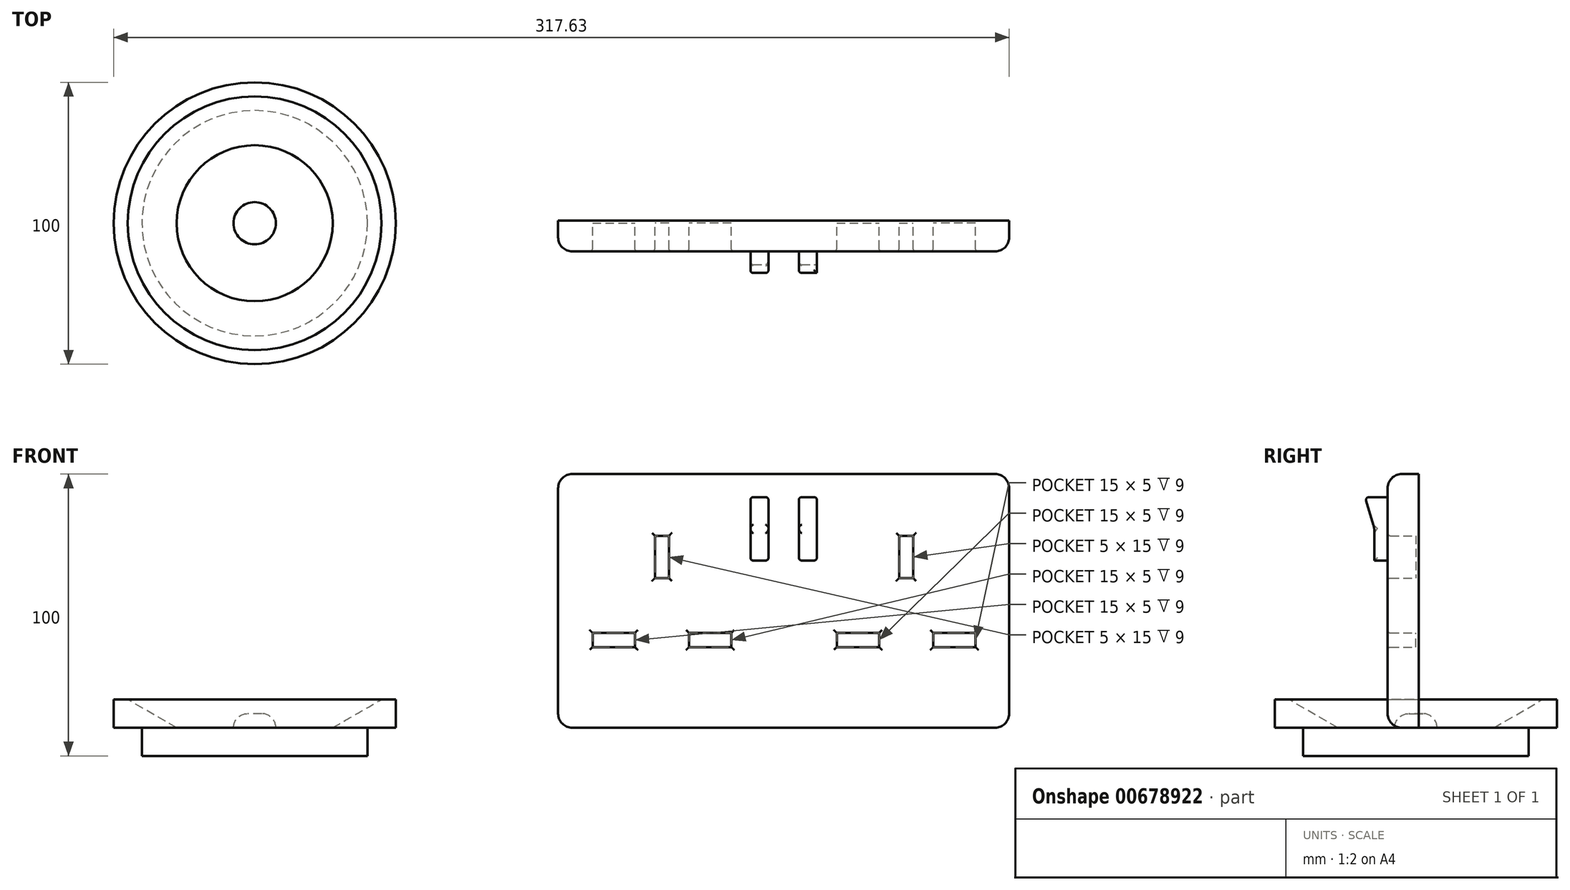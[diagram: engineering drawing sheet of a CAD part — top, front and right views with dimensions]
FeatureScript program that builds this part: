
annotation { "Feature Type Name" : "Feature", "Feature Type Description" : "" }
export const myFeature = defineFeature(function(context is Context, id is Id, definition is map)
    precondition{}
    {
        {
            var Q0;
            Q0=qCreatedBy(makeId("Top.planeOp"),FACE);
            var sketch = newSketch(context, id + "F0", { "sketchPlane" : qUnion([Q0])});
            skCircle(sketch, "E0", {"center": v(0, 0) * mm, "radius": 50 * mm});
            skSolve(sketch);
        }
        {
            var Q0;
            Q0=qSketchRegion(id+"F0",true);
            extrude(context, id + "F1", {"entities" : qUnion([Q0]), "depth" : 10 * mm, "offsetDistance" : 25 * mm});
        }
        {
            var Q0;
            Q0=makeQuery(id+"F1.opExtrude","CAP_FACE",FACE,{"disambiguationData":[OSD([sQuery(id+"F0.wireOp",EDGE,"E0")])],"isStart":true});
            var sketch = newSketch(context, id + "F2", { "sketchPlane" : qUnion([Q0])});
            skCircle(sketch, "E1", {"center": v(0, 0) * mm, "radius": 40 * mm});
            skSolve(sketch);
        }
        {
            var Q0;
            Q0=qSketchRegion(id+"F2",true);
            extrude(context, id + "F3", {"entities" : qUnion([Q0]), "operationType" : NewBodyOperationType.ADD, "depth" : 10 * mm, "offsetDistance" : 25 * mm});
        }
        {
            var Q0;
            Q0=makeQuery(id+"F1.opExtrude","CAP_FACE",FACE,{"disambiguationData":[OSD([sQuery(id+"F0.wireOp",EDGE,"E0")])],"isStart":false});
            var sketch = newSketch(context, id + "F4", { "sketchPlane" : qUnion([Q0])});
            skCircle(sketch, "E2", {"center": v(0, 0) * mm, "radius": 45 * mm});
            skSolve(sketch);
        }
        {
            var Q0;
            Q0=qSketchRegion(id+"F4",true);
            extrude(context, id + "F5", {"entities" : qUnion([Q0]), "operationType" : NewBodyOperationType.REMOVE, "oppositeDirection" : true, "depth" : 10 * mm, "offsetDistance" : 25 * mm, "hasDraft" : true, "draftAngle" : 60 * degree, "draftPullDirection" : true});
        }
        {
            var Q0;
            Q0=makeQuery(id+"F5.boolean.opBoolean","COPY",FACE,{"derivedFrom":makeQuery(id+"F5.opExtrude","CAP_FACE",FACE,{"disambiguationData":[OSD([sQuery(id+"F4.wireOp",EDGE,"E2")])],"isStart":false})});
            var sketch = newSketch(context, id + "F6", { "sketchPlane" : qUnion([Q0])});
            skCircle(sketch, "E3", {"center": v(0, 0) * mm, "radius": 7.5 * mm});
            skSolve(sketch);
        }
        {
            var Q0;
            Q0=qSketchRegion(id+"F6",true);
            extrude(context, id + "F7", {"entities" : qUnion([Q0]), "operationType" : NewBodyOperationType.ADD, "depth" : 5 * mm, "offsetDistance" : 25 * mm});
        }
        {
            var Q0;
            Q0=makeQuery(id+"F7.opExtrude","CAP_EDGE",EDGE,{"disambiguationData":[OSD([sQuery(id+"F6.wireOp",EDGE,"E3")])],"isStart":false});
            fillet(context, id + "F8", {"entities" : qUnion([Q0]), "radius" : 5 * mm, "tangentPropagation" : true, "allowEdgeOverflow" : false});
        }
        {
            var Q0;
            Q0=qCreatedBy(makeId("Front.planeOp"),FACE);
            var sketch = newSketch(context, id + "F9", { "sketchPlane" : qUnion([Q0])});
            skLineSegment(sketch, "E4.bottom", {"start": v(107.63, 0) * mm, "end": v(267.63, 0) * mm});
            skLineSegment(sketch, "E4.top", {"start": v(107.63, 90) * mm, "end": v(267.63, 90) * mm});
            skLineSegment(sketch, "E4.left", {"start": v(107.63, 0) * mm, "end": v(107.63, 90) * mm});
            skLineSegment(sketch, "E4.right", {"start": v(267.63, 0) * mm, "end": v(267.63, 90) * mm});
            skSolve(sketch);
        }
        {
            var Q0;
            Q0=qSketchRegion(id+"F9",true);
            extrude(context, id + "F10", {"entities" : qUnion([Q0]), "depth" : 10 * mm, "offsetDistance" : 25 * mm});
        }
        {
            var Q0;
            Q0=qCreatedBy(makeId("Front.planeOp"),FACE);
            var sketch = newSketch(context, id + "F11", { "sketchPlane" : qUnion([Q0])});
            skLineSegment(sketch, "E5.bottom", {"start": v(146.96, 68.1) * mm, "end": v(141.96, 68.1) * mm});
            skLineSegment(sketch, "E5.top", {"start": v(146.96, 53.1) * mm, "end": v(141.96, 53.1) * mm});
            skLineSegment(sketch, "E5.left", {"start": v(146.96, 68.1) * mm, "end": v(146.96, 53.1) * mm});
            skLineSegment(sketch, "E5.right", {"start": v(141.96, 68.1) * mm, "end": v(141.96, 53.1) * mm});
            skPoint(sketch, "E5.middle", {"position": v(144.46, 60.6) * mm});
            skLineSegment(sketch, "E6.bottom", {"start": v(119.85, 28.62) * mm, "end": v(134.85, 28.62) * mm});
            skLineSegment(sketch, "E6.top", {"start": v(119.85, 33.62) * mm, "end": v(134.85, 33.62) * mm});
            skLineSegment(sketch, "E6.left", {"start": v(119.85, 28.62) * mm, "end": v(119.85, 33.62) * mm});
            skLineSegment(sketch, "E6.right", {"start": v(134.85, 28.62) * mm, "end": v(134.85, 33.62) * mm});
            skPoint(sketch, "E6.middle", {"position": v(127.35, 31.12) * mm});
            skLineSegment(sketch, "E7.bottom", {"start": v(169.06, 28.62) * mm, "end": v(154.06, 28.62) * mm});
            skLineSegment(sketch, "E7.top", {"start": v(169.06, 33.62) * mm, "end": v(154.06, 33.62) * mm});
            skLineSegment(sketch, "E7.left", {"start": v(169.06, 28.62) * mm, "end": v(169.06, 33.62) * mm});
            skLineSegment(sketch, "E7.right", {"start": v(154.06, 28.62) * mm, "end": v(154.06, 33.62) * mm});
            skPoint(sketch, "E7.middle", {"position": v(161.56, 31.12) * mm});
            skPoint(sketch, "E8", {"position": v(134.85, 31.12) * mm});
            skLineSegment(sketch, "E9.MirrorCS", {"start": v(228.58, 68.1) * mm, "end": v(228.58, 53.1) * mm});
            skLineSegment(sketch, "E10.MirrorCS", {"start": v(228.58, 68.1) * mm, "end": v(233.58, 68.1) * mm});
            skLineSegment(sketch, "E11.MirrorCS", {"start": v(233.58, 68.1) * mm, "end": v(233.58, 53.1) * mm});
            skLineSegment(sketch, "E12.MirrorCS", {"start": v(228.58, 53.1) * mm, "end": v(233.58, 53.1) * mm});
            skLineSegment(sketch, "E13.MirrorCS", {"start": v(206.47, 28.62) * mm, "end": v(221.47, 28.62) * mm});
            skLineSegment(sketch, "E14.MirrorCS", {"start": v(206.47, 33.62) * mm, "end": v(221.47, 33.62) * mm});
            skLineSegment(sketch, "E15.MirrorCS", {"start": v(221.47, 28.62) * mm, "end": v(221.47, 33.62) * mm});
            skLineSegment(sketch, "E16.MirrorCS", {"start": v(206.47, 28.62) * mm, "end": v(206.47, 33.62) * mm});
            skPoint(sketch, "E17.MirrorP", {"position": v(213.97, 31.12) * mm});
            skLineSegment(sketch, "E18.MirrorCS", {"start": v(240.68, 28.62) * mm, "end": v(240.68, 33.62) * mm});
            skLineSegment(sketch, "E19.MirrorCS", {"start": v(255.68, 28.62) * mm, "end": v(255.68, 33.62) * mm});
            skLineSegment(sketch, "E20.MirrorCS", {"start": v(255.68, 28.62) * mm, "end": v(240.68, 28.62) * mm});
            skLineSegment(sketch, "E21.MirrorCS", {"start": v(255.68, 33.62) * mm, "end": v(240.68, 33.62) * mm});
            skPoint(sketch, "E22.MirrorP", {"position": v(248.18, 31.12) * mm});
            skPoint(sketch, "E23.MirrorP", {"position": v(240.68, 31.12) * mm});
            skSolve(sketch);
        }
        {
            var Q0;
            Q0=qSketchRegion(id+"F11",true);
            extrude(context, id + "F12", {"entities" : qUnion([Q0]), "operationType" : NewBodyOperationType.REMOVE, "depth" : 15 * mm, "offsetDistance" : 25 * mm});
        }
        {
            var Q0;
            Q0=makeQuery(id+"F10.opExtrude","CAP_FACE",FACE,{"disambiguationData":[OSD([sQuery(id+"F9.wireOp",EDGE,"E4.bottom"),sQuery(id+"F9.wireOp",EDGE,"E4.top"),sQuery(id+"F9.wireOp",EDGE,"E4.left"),sQuery(id+"F9.wireOp",EDGE,"E4.right")])],"isStart":false});
            var sketch = newSketch(context, id + "F13", { "sketchPlane" : qUnion([Q0])});
            skLineSegment(sketch, "E24.bottom", {"start": v(193.04, 81.81) * mm, "end": v(199.4, 81.81) * mm});
            skLineSegment(sketch, "E24.top", {"start": v(193.04, 59.31) * mm, "end": v(199.4, 59.31) * mm});
            skLineSegment(sketch, "E24.left", {"start": v(193.04, 81.81) * mm, "end": v(193.04, 59.31) * mm});
            skLineSegment(sketch, "E24.right", {"start": v(199.4, 81.81) * mm, "end": v(199.4, 59.31) * mm});
            skLineSegment(sketch, "E25.MirrorCS", {"start": v(182.22, 81.81) * mm, "end": v(175.86, 81.81) * mm});
            skLineSegment(sketch, "E26.MirrorCS", {"start": v(182.22, 81.81) * mm, "end": v(182.22, 59.31) * mm});
            skLineSegment(sketch, "E27.MirrorCS", {"start": v(175.86, 81.81) * mm, "end": v(175.86, 59.31) * mm});
            skLineSegment(sketch, "E28.MirrorCS", {"start": v(182.22, 59.31) * mm, "end": v(175.86, 59.31) * mm});
            skSolve(sketch);
        }
        {
            var Q0;
            Q0=qSketchRegion(id+"F13",true);
            extrude(context, id + "F14", {"entities" : qUnion([Q0]), "operationType" : NewBodyOperationType.ADD, "depth" : 8 * mm, "offsetDistance" : 25 * mm});
        }
        {
            var Q0;
            Q0=makeQuery(id+"F14.opExtrude","SWEPT_FACE",FACE,{"disambiguationData":[OSD([sQuery(id+"F13.wireOp",EDGE,"E24.right")])]});
            var sketch = newSketch(context, id + "F15", { "sketchPlane" : qUnion([Q0])});
            skLineSegment(sketch, "E29", {"start": v(-14.66, 70.56) * mm, "end": v(-18, 81.81) * mm});
            skLineSegment(sketch, "E30", {"start": v(-14.66, 70.56) * mm, "end": v(-14.66, 59.31) * mm});
            skPoint(sketch, "E30.endSnap0", {"position": v(-14, 59.31) * mm});
            skLineSegment(sketch, "E31", {"start": v(-14.66, 59.31) * mm, "end": v(-18, 59.31) * mm});
            skLineSegment(sketch, "E32", {"start": v(-18, 59.31) * mm, "end": v(-18, 81.81) * mm});
            skSolve(sketch);
        }
        {
            var Q0;
            Q0=qSketchRegion(id+"F15",true);
            extrude(context, id + "F16", {"entities" : qUnion([Q0]), "operationType" : NewBodyOperationType.REMOVE, "oppositeDirection" : true, "depth" : 25 * mm, "offsetDistance" : 25 * mm});
        }
        {
            var Q0;
            Q0=makeQuery(id+"F16.boolean.opBoolean","COPY",EDGE,{"derivedFrom":makeQuery(id+"F16.opExtrude","CAP_EDGE",EDGE,{"disambiguationData":[OSD([sQuery(id+"F15.wireOp",EDGE,"E30")])],"isStart":true})});
            var Q1;
            Q1=makeQuery(id+"F16.boolean.opBoolean","COPY",EDGE,{"derivedFrom":makeQuery(id+"F16.opExtrude","CAP_EDGE",EDGE,{"disambiguationData":[OSD([sQuery(id+"F15.wireOp",EDGE,"E29")])],"isStart":true})});
            var Q2;
            {var subQ0=sQuery(id+"F13.wireOp",EDGE,"E24.bottom");Q2=makeQuery(id+"F16.boolean.opBoolean","MERGE",EDGE,{"derivedFrom":[makeQuery(id+"F14.opExtrude","CAP_EDGE",EDGE,{"disambiguationData":[OSD([subQ0])],"isStart":false}),makeQuery(id+"F16.opExtrude","SWEPT_EDGE",EDGE,{"disambiguationData":[OSD([subQ0,sQuery(id+"F13.wireOp",EDGE,"E24.right"),sQuery(id+"F15.wireOp",EDGE,"E29"),sQuery(id+"F15.wireOp",EDGE,"E32")])]})]});}
            var Q3;
            Q3=makeQuery(id+"F16.boolean.opBoolean","INTERSECT",EDGE,{"derivedFrom":[makeQuery(id+"F14.opExtrude","SWEPT_FACE",FACE,{"disambiguationData":[OSD([sQuery(id+"F13.wireOp",EDGE,"E24.left")])]}),makeQuery(id+"F16.opExtrude","SWEPT_FACE",FACE,{"disambiguationData":[OSD([sQuery(id+"F15.wireOp",EDGE,"E29")])]})]});
            var Q4;
            Q4=makeQuery(id+"F16.boolean.opBoolean","INTERSECT",EDGE,{"derivedFrom":[makeQuery(id+"F14.opExtrude","SWEPT_FACE",FACE,{"disambiguationData":[OSD([sQuery(id+"F13.wireOp",EDGE,"E24.left")])]}),makeQuery(id+"F16.opExtrude","SWEPT_FACE",FACE,{"disambiguationData":[OSD([sQuery(id+"F15.wireOp",EDGE,"E30")])]})]});
            var Q5;
            {var subQ0=sQuery(id+"F13.wireOp",EDGE,"E24.top");var subQ1=sQuery(id+"F15.wireOp",EDGE,"E30");Q5=makeQuery(id+"F16.boolean.opBoolean","COPY",EDGE,{"disambiguationData":[topologyDisambiguationEdgeConnected([makeQuery(id+"F14.opExtrude","SWEPT_FACE",FACE,{"disambiguationData":[OSD([subQ0])]})])],"derivedFrom":makeQuery(id+"F16.opExtrude","SWEPT_EDGE",EDGE,{"disambiguationData":[OSD([subQ0,sQuery(id+"F13.wireOp",EDGE,"E24.right"),subQ1,sQuery(id+"F15.wireOp",EDGE,"E31")])]})});}
            var Q6;
            Q6=makeQuery(id+"F14.opExtrude","SWEPT_EDGE",EDGE,{"disambiguationData":[OSD([sQuery(id+"F13.wireOp",EDGE,"E24.bottom"),sQuery(id+"F13.wireOp",EDGE,"E24.right")])]});
            var Q7;
            Q7=makeQuery(id+"F14.opExtrude","SWEPT_EDGE",EDGE,{"disambiguationData":[OSD([sQuery(id+"F13.wireOp",EDGE,"E24.top"),sQuery(id+"F13.wireOp",EDGE,"E24.right")])]});
            var Q8;
            Q8=makeQuery(id+"F14.opExtrude","SWEPT_EDGE",EDGE,{"disambiguationData":[OSD([sQuery(id+"F13.wireOp",EDGE,"E24.top"),sQuery(id+"F13.wireOp",EDGE,"E24.left")])]});
            var Q9;
            Q9=makeQuery(id+"F14.opExtrude","SWEPT_EDGE",EDGE,{"disambiguationData":[OSD([sQuery(id+"F13.wireOp",EDGE,"E24.bottom"),sQuery(id+"F13.wireOp",EDGE,"E24.left")])]});
            var Q10;
            Q10=makeQuery(id+"F16.boolean.opBoolean","INTERSECT",EDGE,{"derivedFrom":[makeQuery(id+"F14.opExtrude","SWEPT_FACE",FACE,{"disambiguationData":[OSD([sQuery(id+"F13.wireOp",EDGE,"E26.MirrorCS")])]}),makeQuery(id+"F16.opExtrude","SWEPT_FACE",FACE,{"disambiguationData":[OSD([sQuery(id+"F15.wireOp",EDGE,"E30")])]})]});
            var Q11;
            Q11=makeQuery(id+"F16.boolean.opBoolean","INTERSECT",EDGE,{"derivedFrom":[makeQuery(id+"F14.opExtrude","SWEPT_FACE",FACE,{"disambiguationData":[OSD([sQuery(id+"F13.wireOp",EDGE,"E26.MirrorCS")])]}),makeQuery(id+"F16.opExtrude","SWEPT_FACE",FACE,{"disambiguationData":[OSD([sQuery(id+"F15.wireOp",EDGE,"E29")])]})]});
            var Q12;
            Q12=makeQuery(id+"F16.boolean.opBoolean","MERGE",EDGE,{"derivedFrom":[makeQuery(id+"F14.opExtrude","CAP_EDGE",EDGE,{"disambiguationData":[OSD([sQuery(id+"F13.wireOp",EDGE,"E25.MirrorCS")])],"isStart":false}),makeQuery(id+"F16.opExtrude","SWEPT_EDGE",EDGE,{"disambiguationData":[OSD([sQuery(id+"F13.wireOp",EDGE,"E24.bottom"),sQuery(id+"F13.wireOp",EDGE,"E24.right"),sQuery(id+"F15.wireOp",EDGE,"E29"),sQuery(id+"F15.wireOp",EDGE,"E32")])]})]});
            var Q13;
            Q13=makeQuery(id+"F16.boolean.opBoolean","INTERSECT",EDGE,{"derivedFrom":[makeQuery(id+"F14.opExtrude","SWEPT_FACE",FACE,{"disambiguationData":[OSD([sQuery(id+"F13.wireOp",EDGE,"E27.MirrorCS")])]}),makeQuery(id+"F16.opExtrude","SWEPT_FACE",FACE,{"disambiguationData":[OSD([sQuery(id+"F15.wireOp",EDGE,"E29")])]})]});
            var Q14;
            Q14=makeQuery(id+"F16.boolean.opBoolean","INTERSECT",EDGE,{"derivedFrom":[makeQuery(id+"F14.opExtrude","SWEPT_FACE",FACE,{"disambiguationData":[OSD([sQuery(id+"F13.wireOp",EDGE,"E27.MirrorCS")])]}),makeQuery(id+"F16.opExtrude","SWEPT_FACE",FACE,{"disambiguationData":[OSD([sQuery(id+"F15.wireOp",EDGE,"E30")])]})]});
            var Q15;
            {var subQ0=sQuery(id+"F15.wireOp",EDGE,"E30");Q15=makeQuery(id+"F16.boolean.opBoolean","COPY",EDGE,{"disambiguationData":[topologyDisambiguationEdgeConnected([makeQuery(id+"F14.opExtrude","SWEPT_FACE",FACE,{"disambiguationData":[OSD([sQuery(id+"F13.wireOp",EDGE,"E28.MirrorCS")])]})])],"derivedFrom":makeQuery(id+"F16.opExtrude","SWEPT_EDGE",EDGE,{"disambiguationData":[OSD([sQuery(id+"F13.wireOp",EDGE,"E24.top"),sQuery(id+"F13.wireOp",EDGE,"E24.right"),subQ0,sQuery(id+"F15.wireOp",EDGE,"E31")])]})});}
            var Q16;
            Q16=makeQuery(id+"F14.opExtrude","SWEPT_EDGE",EDGE,{"disambiguationData":[OSD([sQuery(id+"F13.wireOp",EDGE,"E27.MirrorCS"),sQuery(id+"F13.wireOp",EDGE,"E28.MirrorCS")])]});
            var Q17;
            Q17=makeQuery(id+"F14.opExtrude","SWEPT_EDGE",EDGE,{"disambiguationData":[OSD([sQuery(id+"F13.wireOp",EDGE,"E26.MirrorCS"),sQuery(id+"F13.wireOp",EDGE,"E28.MirrorCS")])]});
            var Q18;
            Q18=makeQuery(id+"F14.opExtrude","SWEPT_EDGE",EDGE,{"disambiguationData":[OSD([sQuery(id+"F13.wireOp",EDGE,"E25.MirrorCS"),sQuery(id+"F13.wireOp",EDGE,"E26.MirrorCS")])]});
            var Q19;
            Q19=makeQuery(id+"F14.opExtrude","SWEPT_EDGE",EDGE,{"disambiguationData":[OSD([sQuery(id+"F13.wireOp",EDGE,"E25.MirrorCS"),sQuery(id+"F13.wireOp",EDGE,"E27.MirrorCS")])]});
            fillet(context, id + "F17", {"entities" : qUnion([Q0, Q1, Q2, Q3, Q4, Q5, Q6, Q7, Q8, Q9, Q10, Q11, Q12, Q13, Q14, Q15, Q16, Q17, Q18, Q19]), "radius" : 1 * mm, "tangentPropagation" : true, "allowEdgeOverflow" : false});
        }
        {
            var Q0;
            {var subQ0=sQuery(id+"F15.wireOp",EDGE,"E29");var subQ1=sQuery(id+"F15.wireOp",EDGE,"E30");Q0=makeQuery(id+"F16.boolean.opBoolean","COPY",EDGE,{"disambiguationData":[TD([makeQuery(id+"F14.opExtrude","SWEPT_FACE",FACE,{"disambiguationData":[OSD([sQuery(id+"F13.wireOp",EDGE,"E26.MirrorCS")])]})])],"derivedFrom":makeQuery(id+"F16.opExtrude","SWEPT_EDGE",EDGE,{"disambiguationData":[OSD([subQ0,subQ1])]})});}
            var Q1;
            {var subQ0=sQuery(id+"F15.wireOp",EDGE,"E29");var subQ1=sQuery(id+"F15.wireOp",EDGE,"E30");Q1=makeQuery(id+"F16.boolean.opBoolean","COPY",EDGE,{"disambiguationData":[TD([makeQuery(id+"F14.opExtrude","SWEPT_FACE",FACE,{"disambiguationData":[OSD([sQuery(id+"F13.wireOp",EDGE,"E24.left")])]})])],"derivedFrom":makeQuery(id+"F16.opExtrude","SWEPT_EDGE",EDGE,{"disambiguationData":[OSD([subQ0,subQ1])]})});}
            fillet(context, id + "F18", {"entities" : qUnion([Q0, Q1]), "radius" : 10 * mm, "tangentPropagation" : true, "allowEdgeOverflow" : false});
        }
        {
            var Q0;
            Q0=makeQuery(id+"F12.boolean.opBoolean","INTERSECT",EDGE,{"derivedFrom":[makeQuery(id+"F10.opExtrude","CAP_FACE",FACE,{"disambiguationData":[OSD([sQuery(id+"F9.wireOp",EDGE,"E4.bottom"),sQuery(id+"F9.wireOp",EDGE,"E4.top"),sQuery(id+"F9.wireOp",EDGE,"E4.left"),sQuery(id+"F9.wireOp",EDGE,"E4.right")])],"isStart":false}),makeQuery(id+"F12.opExtrude","SWEPT_FACE",FACE,{"disambiguationData":[OSD([sQuery(id+"F11.wireOp",EDGE,"E5.right")])]})]});
            var Q1;
            Q1=makeQuery(id+"F12.boolean.opBoolean","INTERSECT",EDGE,{"derivedFrom":[makeQuery(id+"F10.opExtrude","CAP_FACE",FACE,{"disambiguationData":[OSD([sQuery(id+"F9.wireOp",EDGE,"E4.bottom"),sQuery(id+"F9.wireOp",EDGE,"E4.top"),sQuery(id+"F9.wireOp",EDGE,"E4.left"),sQuery(id+"F9.wireOp",EDGE,"E4.right")])],"isStart":false}),makeQuery(id+"F12.opExtrude","SWEPT_FACE",FACE,{"disambiguationData":[OSD([sQuery(id+"F11.wireOp",EDGE,"E5.top")])]})]});
            var Q2;
            Q2=makeQuery(id+"F12.boolean.opBoolean","INTERSECT",EDGE,{"derivedFrom":[makeQuery(id+"F10.opExtrude","CAP_FACE",FACE,{"disambiguationData":[OSD([sQuery(id+"F9.wireOp",EDGE,"E4.bottom"),sQuery(id+"F9.wireOp",EDGE,"E4.top"),sQuery(id+"F9.wireOp",EDGE,"E4.left"),sQuery(id+"F9.wireOp",EDGE,"E4.right")])],"isStart":false}),makeQuery(id+"F12.opExtrude","SWEPT_FACE",FACE,{"disambiguationData":[OSD([sQuery(id+"F11.wireOp",EDGE,"E5.left")])]})]});
            var Q3;
            Q3=makeQuery(id+"F12.boolean.opBoolean","INTERSECT",EDGE,{"derivedFrom":[makeQuery(id+"F10.opExtrude","CAP_FACE",FACE,{"disambiguationData":[OSD([sQuery(id+"F9.wireOp",EDGE,"E4.bottom"),sQuery(id+"F9.wireOp",EDGE,"E4.top"),sQuery(id+"F9.wireOp",EDGE,"E4.left"),sQuery(id+"F9.wireOp",EDGE,"E4.right")])],"isStart":false}),makeQuery(id+"F12.opExtrude","SWEPT_FACE",FACE,{"disambiguationData":[OSD([sQuery(id+"F11.wireOp",EDGE,"E5.bottom")])]})]});
            var Q4;
            Q4=makeQuery(id+"F12.boolean.opBoolean","INTERSECT",EDGE,{"derivedFrom":[makeQuery(id+"F10.opExtrude","CAP_FACE",FACE,{"disambiguationData":[OSD([sQuery(id+"F9.wireOp",EDGE,"E4.bottom"),sQuery(id+"F9.wireOp",EDGE,"E4.top"),sQuery(id+"F9.wireOp",EDGE,"E4.left"),sQuery(id+"F9.wireOp",EDGE,"E4.right")])],"isStart":false}),makeQuery(id+"F12.opExtrude","SWEPT_FACE",FACE,{"disambiguationData":[OSD([sQuery(id+"F11.wireOp",EDGE,"E6.top")])]})]});
            var Q5;
            Q5=makeQuery(id+"F12.boolean.opBoolean","INTERSECT",EDGE,{"derivedFrom":[makeQuery(id+"F10.opExtrude","CAP_FACE",FACE,{"disambiguationData":[OSD([sQuery(id+"F9.wireOp",EDGE,"E4.bottom"),sQuery(id+"F9.wireOp",EDGE,"E4.top"),sQuery(id+"F9.wireOp",EDGE,"E4.left"),sQuery(id+"F9.wireOp",EDGE,"E4.right")])],"isStart":false}),makeQuery(id+"F12.opExtrude","SWEPT_FACE",FACE,{"disambiguationData":[OSD([sQuery(id+"F11.wireOp",EDGE,"E6.left")])]})]});
            var Q6;
            Q6=makeQuery(id+"F12.boolean.opBoolean","INTERSECT",EDGE,{"derivedFrom":[makeQuery(id+"F10.opExtrude","CAP_FACE",FACE,{"disambiguationData":[OSD([sQuery(id+"F9.wireOp",EDGE,"E4.bottom"),sQuery(id+"F9.wireOp",EDGE,"E4.top"),sQuery(id+"F9.wireOp",EDGE,"E4.left"),sQuery(id+"F9.wireOp",EDGE,"E4.right")])],"isStart":false}),makeQuery(id+"F12.opExtrude","SWEPT_FACE",FACE,{"disambiguationData":[OSD([sQuery(id+"F11.wireOp",EDGE,"E6.bottom")])]})]});
            var Q7;
            Q7=makeQuery(id+"F12.boolean.opBoolean","INTERSECT",EDGE,{"derivedFrom":[makeQuery(id+"F10.opExtrude","CAP_FACE",FACE,{"disambiguationData":[OSD([sQuery(id+"F9.wireOp",EDGE,"E4.bottom"),sQuery(id+"F9.wireOp",EDGE,"E4.top"),sQuery(id+"F9.wireOp",EDGE,"E4.left"),sQuery(id+"F9.wireOp",EDGE,"E4.right")])],"isStart":false}),makeQuery(id+"F12.opExtrude","SWEPT_FACE",FACE,{"disambiguationData":[OSD([sQuery(id+"F11.wireOp",EDGE,"E6.right")])]})]});
            var Q8;
            Q8=makeQuery(id+"F12.boolean.opBoolean","INTERSECT",EDGE,{"derivedFrom":[makeQuery(id+"F10.opExtrude","CAP_FACE",FACE,{"disambiguationData":[OSD([sQuery(id+"F9.wireOp",EDGE,"E4.bottom"),sQuery(id+"F9.wireOp",EDGE,"E4.top"),sQuery(id+"F9.wireOp",EDGE,"E4.left"),sQuery(id+"F9.wireOp",EDGE,"E4.right")])],"isStart":false}),makeQuery(id+"F12.opExtrude","SWEPT_FACE",FACE,{"disambiguationData":[OSD([sQuery(id+"F11.wireOp",EDGE,"E7.right")])]})]});
            var Q9;
            Q9=makeQuery(id+"F12.boolean.opBoolean","INTERSECT",EDGE,{"derivedFrom":[makeQuery(id+"F10.opExtrude","CAP_FACE",FACE,{"disambiguationData":[OSD([sQuery(id+"F9.wireOp",EDGE,"E4.bottom"),sQuery(id+"F9.wireOp",EDGE,"E4.top"),sQuery(id+"F9.wireOp",EDGE,"E4.left"),sQuery(id+"F9.wireOp",EDGE,"E4.right")])],"isStart":false}),makeQuery(id+"F12.opExtrude","SWEPT_FACE",FACE,{"disambiguationData":[OSD([sQuery(id+"F11.wireOp",EDGE,"E7.top")])]})]});
            var Q10;
            Q10=makeQuery(id+"F12.boolean.opBoolean","INTERSECT",EDGE,{"derivedFrom":[makeQuery(id+"F10.opExtrude","CAP_FACE",FACE,{"disambiguationData":[OSD([sQuery(id+"F9.wireOp",EDGE,"E4.bottom"),sQuery(id+"F9.wireOp",EDGE,"E4.top"),sQuery(id+"F9.wireOp",EDGE,"E4.left"),sQuery(id+"F9.wireOp",EDGE,"E4.right")])],"isStart":false}),makeQuery(id+"F12.opExtrude","SWEPT_FACE",FACE,{"disambiguationData":[OSD([sQuery(id+"F11.wireOp",EDGE,"E7.left")])]})]});
            var Q11;
            Q11=makeQuery(id+"F12.boolean.opBoolean","INTERSECT",EDGE,{"derivedFrom":[makeQuery(id+"F10.opExtrude","CAP_FACE",FACE,{"disambiguationData":[OSD([sQuery(id+"F9.wireOp",EDGE,"E4.bottom"),sQuery(id+"F9.wireOp",EDGE,"E4.top"),sQuery(id+"F9.wireOp",EDGE,"E4.left"),sQuery(id+"F9.wireOp",EDGE,"E4.right")])],"isStart":false}),makeQuery(id+"F12.opExtrude","SWEPT_FACE",FACE,{"disambiguationData":[OSD([sQuery(id+"F11.wireOp",EDGE,"E7.bottom")])]})]});
            var Q12;
            Q12=makeQuery(id+"F12.boolean.opBoolean","INTERSECT",EDGE,{"derivedFrom":[makeQuery(id+"F10.opExtrude","CAP_FACE",FACE,{"disambiguationData":[OSD([sQuery(id+"F9.wireOp",EDGE,"E4.bottom"),sQuery(id+"F9.wireOp",EDGE,"E4.top"),sQuery(id+"F9.wireOp",EDGE,"E4.left"),sQuery(id+"F9.wireOp",EDGE,"E4.right")])],"isStart":false}),makeQuery(id+"F12.opExtrude","SWEPT_FACE",FACE,{"disambiguationData":[OSD([sQuery(id+"F11.wireOp",EDGE,"E13.MirrorCS")])]})]});
            var Q13;
            Q13=makeQuery(id+"F12.boolean.opBoolean","INTERSECT",EDGE,{"derivedFrom":[makeQuery(id+"F10.opExtrude","CAP_FACE",FACE,{"disambiguationData":[OSD([sQuery(id+"F9.wireOp",EDGE,"E4.bottom"),sQuery(id+"F9.wireOp",EDGE,"E4.top"),sQuery(id+"F9.wireOp",EDGE,"E4.left"),sQuery(id+"F9.wireOp",EDGE,"E4.right")])],"isStart":false}),makeQuery(id+"F12.opExtrude","SWEPT_FACE",FACE,{"disambiguationData":[OSD([sQuery(id+"F11.wireOp",EDGE,"E14.MirrorCS")])]})]});
            var Q14;
            Q14=makeQuery(id+"F12.boolean.opBoolean","INTERSECT",EDGE,{"derivedFrom":[makeQuery(id+"F10.opExtrude","CAP_FACE",FACE,{"disambiguationData":[OSD([sQuery(id+"F9.wireOp",EDGE,"E4.bottom"),sQuery(id+"F9.wireOp",EDGE,"E4.top"),sQuery(id+"F9.wireOp",EDGE,"E4.left"),sQuery(id+"F9.wireOp",EDGE,"E4.right")])],"isStart":false}),makeQuery(id+"F12.opExtrude","SWEPT_FACE",FACE,{"disambiguationData":[OSD([sQuery(id+"F11.wireOp",EDGE,"E16.MirrorCS")])]})]});
            var Q15;
            Q15=makeQuery(id+"F12.boolean.opBoolean","INTERSECT",EDGE,{"derivedFrom":[makeQuery(id+"F10.opExtrude","CAP_FACE",FACE,{"disambiguationData":[OSD([sQuery(id+"F9.wireOp",EDGE,"E4.bottom"),sQuery(id+"F9.wireOp",EDGE,"E4.top"),sQuery(id+"F9.wireOp",EDGE,"E4.left"),sQuery(id+"F9.wireOp",EDGE,"E4.right")])],"isStart":false}),makeQuery(id+"F12.opExtrude","SWEPT_FACE",FACE,{"disambiguationData":[OSD([sQuery(id+"F11.wireOp",EDGE,"E15.MirrorCS")])]})]});
            var Q16;
            Q16=makeQuery(id+"F12.boolean.opBoolean","INTERSECT",EDGE,{"derivedFrom":[makeQuery(id+"F10.opExtrude","CAP_FACE",FACE,{"disambiguationData":[OSD([sQuery(id+"F9.wireOp",EDGE,"E4.bottom"),sQuery(id+"F9.wireOp",EDGE,"E4.top"),sQuery(id+"F9.wireOp",EDGE,"E4.left"),sQuery(id+"F9.wireOp",EDGE,"E4.right")])],"isStart":false}),makeQuery(id+"F12.opExtrude","SWEPT_FACE",FACE,{"disambiguationData":[OSD([sQuery(id+"F11.wireOp",EDGE,"E21.MirrorCS")])]})]});
            var Q17;
            Q17=makeQuery(id+"F12.boolean.opBoolean","INTERSECT",EDGE,{"derivedFrom":[makeQuery(id+"F10.opExtrude","CAP_FACE",FACE,{"disambiguationData":[OSD([sQuery(id+"F9.wireOp",EDGE,"E4.bottom"),sQuery(id+"F9.wireOp",EDGE,"E4.top"),sQuery(id+"F9.wireOp",EDGE,"E4.left"),sQuery(id+"F9.wireOp",EDGE,"E4.right")])],"isStart":false}),makeQuery(id+"F12.opExtrude","SWEPT_FACE",FACE,{"disambiguationData":[OSD([sQuery(id+"F11.wireOp",EDGE,"E18.MirrorCS")])]})]});
            var Q18;
            Q18=makeQuery(id+"F12.boolean.opBoolean","INTERSECT",EDGE,{"derivedFrom":[makeQuery(id+"F10.opExtrude","CAP_FACE",FACE,{"disambiguationData":[OSD([sQuery(id+"F9.wireOp",EDGE,"E4.bottom"),sQuery(id+"F9.wireOp",EDGE,"E4.top"),sQuery(id+"F9.wireOp",EDGE,"E4.left"),sQuery(id+"F9.wireOp",EDGE,"E4.right")])],"isStart":false}),makeQuery(id+"F12.opExtrude","SWEPT_FACE",FACE,{"disambiguationData":[OSD([sQuery(id+"F11.wireOp",EDGE,"E20.MirrorCS")])]})]});
            var Q19;
            Q19=makeQuery(id+"F12.boolean.opBoolean","INTERSECT",EDGE,{"derivedFrom":[makeQuery(id+"F10.opExtrude","CAP_FACE",FACE,{"disambiguationData":[OSD([sQuery(id+"F9.wireOp",EDGE,"E4.bottom"),sQuery(id+"F9.wireOp",EDGE,"E4.top"),sQuery(id+"F9.wireOp",EDGE,"E4.left"),sQuery(id+"F9.wireOp",EDGE,"E4.right")])],"isStart":false}),makeQuery(id+"F12.opExtrude","SWEPT_FACE",FACE,{"disambiguationData":[OSD([sQuery(id+"F11.wireOp",EDGE,"E19.MirrorCS")])]})]});
            var Q20;
            Q20=makeQuery(id+"F12.boolean.opBoolean","INTERSECT",EDGE,{"derivedFrom":[makeQuery(id+"F10.opExtrude","CAP_FACE",FACE,{"disambiguationData":[OSD([sQuery(id+"F9.wireOp",EDGE,"E4.bottom"),sQuery(id+"F9.wireOp",EDGE,"E4.top"),sQuery(id+"F9.wireOp",EDGE,"E4.left"),sQuery(id+"F9.wireOp",EDGE,"E4.right")])],"isStart":false}),makeQuery(id+"F12.opExtrude","SWEPT_FACE",FACE,{"disambiguationData":[OSD([sQuery(id+"F11.wireOp",EDGE,"E10.MirrorCS")])]})]});
            var Q21;
            Q21=makeQuery(id+"F12.boolean.opBoolean","INTERSECT",EDGE,{"derivedFrom":[makeQuery(id+"F10.opExtrude","CAP_FACE",FACE,{"disambiguationData":[OSD([sQuery(id+"F9.wireOp",EDGE,"E4.bottom"),sQuery(id+"F9.wireOp",EDGE,"E4.top"),sQuery(id+"F9.wireOp",EDGE,"E4.left"),sQuery(id+"F9.wireOp",EDGE,"E4.right")])],"isStart":false}),makeQuery(id+"F12.opExtrude","SWEPT_FACE",FACE,{"disambiguationData":[OSD([sQuery(id+"F11.wireOp",EDGE,"E9.MirrorCS")])]})]});
            var Q22;
            Q22=makeQuery(id+"F12.boolean.opBoolean","INTERSECT",EDGE,{"derivedFrom":[makeQuery(id+"F10.opExtrude","CAP_FACE",FACE,{"disambiguationData":[OSD([sQuery(id+"F9.wireOp",EDGE,"E4.bottom"),sQuery(id+"F9.wireOp",EDGE,"E4.top"),sQuery(id+"F9.wireOp",EDGE,"E4.left"),sQuery(id+"F9.wireOp",EDGE,"E4.right")])],"isStart":false}),makeQuery(id+"F12.opExtrude","SWEPT_FACE",FACE,{"disambiguationData":[OSD([sQuery(id+"F11.wireOp",EDGE,"E12.MirrorCS")])]})]});
            var Q23;
            Q23=makeQuery(id+"F12.boolean.opBoolean","INTERSECT",EDGE,{"derivedFrom":[makeQuery(id+"F10.opExtrude","CAP_FACE",FACE,{"disambiguationData":[OSD([sQuery(id+"F9.wireOp",EDGE,"E4.bottom"),sQuery(id+"F9.wireOp",EDGE,"E4.top"),sQuery(id+"F9.wireOp",EDGE,"E4.left"),sQuery(id+"F9.wireOp",EDGE,"E4.right")])],"isStart":false}),makeQuery(id+"F12.opExtrude","SWEPT_FACE",FACE,{"disambiguationData":[OSD([sQuery(id+"F11.wireOp",EDGE,"E11.MirrorCS")])]})]});
            fillet(context, id + "F19", {"entities" : qUnion([Q0, Q1, Q2, Q3, Q4, Q5, Q6, Q7, Q8, Q9, Q10, Q11, Q12, Q13, Q14, Q15, Q16, Q17, Q18, Q19, Q20, Q21, Q22, Q23]), "radius" : 1 * mm, "tangentPropagation" : true, "allowEdgeOverflow" : false});
        }
        {
            var Q0;
            Q0=makeQuery(id+"F10.opExtrude","SWEPT_EDGE",EDGE,{"disambiguationData":[OSD([sQuery(id+"F9.wireOp",EDGE,"E4.top"),sQuery(id+"F9.wireOp",EDGE,"E4.right")])]});
            var Q1;
            Q1=makeQuery(id+"F10.opExtrude","SWEPT_EDGE",EDGE,{"disambiguationData":[OSD([sQuery(id+"F9.wireOp",EDGE,"E4.top"),sQuery(id+"F9.wireOp",EDGE,"E4.left")])]});
            var Q2;
            Q2=makeQuery(id+"F10.opExtrude","SWEPT_EDGE",EDGE,{"disambiguationData":[OSD([sQuery(id+"F9.wireOp",EDGE,"E4.bottom"),sQuery(id+"F9.wireOp",EDGE,"E4.left")])]});
            var Q3;
            Q3=makeQuery(id+"F10.opExtrude","SWEPT_EDGE",EDGE,{"disambiguationData":[OSD([sQuery(id+"F9.wireOp",EDGE,"E4.bottom"),sQuery(id+"F9.wireOp",EDGE,"E4.right")])]});
            var Q4;
            Q4=makeQuery(id+"F10.opExtrude","CAP_EDGE",EDGE,{"disambiguationData":[OSD([sQuery(id+"F9.wireOp",EDGE,"E4.top")])],"isStart":false});
            var Q5;
            Q5=makeQuery(id+"F10.opExtrude","CAP_EDGE",EDGE,{"disambiguationData":[OSD([sQuery(id+"F9.wireOp",EDGE,"E4.right")])],"isStart":false});
            var Q6;
            Q6=makeQuery(id+"F10.opExtrude","CAP_EDGE",EDGE,{"disambiguationData":[OSD([sQuery(id+"F9.wireOp",EDGE,"E4.bottom")])],"isStart":false});
            var Q7;
            Q7=makeQuery(id+"F10.opExtrude","CAP_EDGE",EDGE,{"disambiguationData":[OSD([sQuery(id+"F9.wireOp",EDGE,"E4.left")])],"isStart":false});
            fillet(context, id + "F20", {"entities" : qUnion([Q0, Q1, Q2, Q3, Q4, Q5, Q6, Q7]), "radius" : 5 * mm, "tangentPropagation" : true, "allowEdgeOverflow" : false});
        }
        {
            var Q0;
            Q0=makeQuery(id+"F10.opExtrude","CAP_FACE",FACE,{"disambiguationData":[OSD([sQuery(id+"F9.wireOp",EDGE,"E4.bottom"),sQuery(id+"F9.wireOp",EDGE,"E4.top"),sQuery(id+"F9.wireOp",EDGE,"E4.left"),sQuery(id+"F9.wireOp",EDGE,"E4.right")])],"isStart":true});
            var sketch = newSketch(context, id + "F21", { "sketchPlane" : qUnion([Q0])});
            skArc(sketch, "E33.0", {"start": v(-112.63, 0) * mm, "mid": v(-109.1, 1.46) * mm, "end": v(-107.63, 5) * mm});
            skLineSegment(sketch, "E33.1", {"start": v(-262.63, 0) * mm, "end": v(-112.63, 0) * mm});
            skLineSegment(sketch, "E33.2", {"start": v(-107.63, 5) * mm, "end": v(-107.63, 85) * mm});
            skArc(sketch, "E33.3", {"start": v(-267.63, 5) * mm, "mid": v(-266.17, 1.46) * mm, "end": v(-262.63, 0) * mm});
            skArc(sketch, "E33.4", {"start": v(-107.63, 85) * mm, "mid": v(-109.1, 88.54) * mm, "end": v(-112.63, 90) * mm});
            skLineSegment(sketch, "E33.5", {"start": v(-112.63, 90) * mm, "end": v(-262.63, 90) * mm});
            skArc(sketch, "E33.6", {"start": v(-262.63, 90) * mm, "mid": v(-266.17, 88.54) * mm, "end": v(-267.63, 85) * mm});
            skLineSegment(sketch, "E33.7", {"start": v(-267.63, 85) * mm, "end": v(-267.63, 5) * mm});
            skSolve(sketch);
        }
        {
            var Q0;
            Q0=qSketchRegion(id+"F21",true);
            extrude(context, id + "F22", {"entities" : qUnion([Q0]), "operationType" : NewBodyOperationType.ADD, "depth" : 1 * mm, "offsetDistance" : 25 * mm});
        }
    });
